annotation { "Feature Type Name" : "Feature", "Feature Type Description" : "" }
export const myFeature = defineFeature(function(context is Context, id is Id, definition is map)
    precondition{}
    {
        {
            var Q0;
            Q0=qCreatedBy(makeId("Top.planeOp"),FACE);
            var sketch = newSketch(context, id + "F0", { "sketchPlane" : qUnion([Q0])});
            skLineSegment(sketch, "E0.bottom", {"start": v(-52.22, 35) * mm, "end": v(51.92, 35) * mm});
            skLineSegment(sketch, "E0.top", {"start": v(-52.22, -33.57) * mm, "end": v(51.92, -33.57) * mm});
            skLineSegment(sketch, "E0.left", {"start": v(-52.22, 35) * mm, "end": v(-52.22, -33.57) * mm});
            skLineSegment(sketch, "E0.right", {"start": v(51.92, 35) * mm, "end": v(51.92, -33.57) * mm});
            skPoint(sketch, "E0.middle", {"position": v(-0.15, 0.72) * mm});
            skLineSegment(sketch, "E1.bottom", {"start": v(-48.41, 31.2) * mm, "end": v(48.1, 31.2) * mm});
            skLineSegment(sketch, "E1.top", {"start": v(-48.41, -29.76) * mm, "end": v(48.1, -29.76) * mm});
            skLineSegment(sketch, "E1.left", {"start": v(-48.41, 31.2) * mm, "end": v(-48.41, -29.76) * mm});
            skLineSegment(sketch, "E1.right", {"start": v(48.1, 31.2) * mm, "end": v(48.1, -29.76) * mm});
            skLineSegment(sketch, "E2", {"start": v(-44.6, 35) * mm, "end": v(-44.6, -33.57) * mm, "construction": true});
            skLineSegment(sketch, "E3", {"start": v(44.3, 31.2) * mm, "end": v(44.3, -33.57) * mm, "construction": true});
            skLineSegment(sketch, "E4", {"start": v(-52.22, 27.39) * mm, "end": v(48.1, 27.39) * mm, "construction": true});
            skLineSegment(sketch, "E5", {"start": v(-52.22, -25.95) * mm, "end": v(51.92, -25.95) * mm, "construction": true});
            skLineSegment(sketch, "E6", {"start": v(-52.22, -33.57) * mm, "end": v(-44.6, -25.95) * mm, "construction": true});
            skCircle(sketch, "E7", {"center": v(-48.41, -29.76) * mm, "radius": 1.52 * mm});
            skLineSegment(sketch, "E8", {"start": v(-52.22, 35) * mm, "end": v(-44.6, 27.39) * mm, "construction": true});
            skCircle(sketch, "E9", {"center": v(-48.41, 31.2) * mm, "radius": 1.52 * mm});
            skLineSegment(sketch, "E10", {"start": v(44.3, 27.39) * mm, "end": v(51.92, 35) * mm, "construction": true});
            skCircle(sketch, "E11", {"center": v(48.1, 31.2) * mm, "radius": 1.52 * mm});
            skLineSegment(sketch, "E12", {"start": v(44.3, -25.95) * mm, "end": v(51.92, -33.57) * mm, "construction": true});
            skCircle(sketch, "E13", {"center": v(48.1, -29.76) * mm, "radius": 1.52 * mm});
            skLineSegment(sketch, "E14", {"start": v(22.7, 35) * mm, "end": v(22.7, -33.57) * mm, "construction": true});
            skLineSegment(sketch, "E15", {"start": v(25.25, 35) * mm, "end": v(25.25, -33.57) * mm, "construction": true});
            skLineSegment(sketch, "E16", {"start": v(26.52, 35) * mm, "end": v(26.52, -33.57) * mm, "construction": true});
            skLineSegment(sketch, "E17", {"start": v(29.06, 35) * mm, "end": v(29.06, -33.57) * mm, "construction": true});
            skLineSegment(sketch, "E18", {"start": v(2.9, 19.77) * mm, "end": v(24.07, 19.77) * mm, "construction": true});
            skLineSegment(sketch, "E19", {"start": v(4.23, -24.68) * mm, "end": v(25.24, -24.68) * mm, "construction": true});
            skLineSegment(sketch, "E20", {"start": v(22.7, -29.76) * mm, "end": v(22.7, -24.68) * mm});
            skLineSegment(sketch, "E21", {"start": v(25.25, -29.76) * mm, "end": v(25.25, -24.68) * mm});
            skLineSegment(sketch, "E22", {"start": v(25.25, -24.68) * mm, "end": v(29.06, -20.87) * mm});
            skLineSegment(sketch, "E23", {"start": v(22.7, -24.68) * mm, "end": v(26.52, -20.87) * mm});
            skLineSegment(sketch, "E24", {"start": v(22.7, 31.2) * mm, "end": v(22.7, 19.77) * mm});
            skLineSegment(sketch, "E25", {"start": v(25.25, 31.2) * mm, "end": v(25.25, 19.77) * mm});
            skLineSegment(sketch, "E26", {"start": v(25.25, 19.77) * mm, "end": v(29.06, 15.96) * mm});
            skLineSegment(sketch, "E27", {"start": v(22.7, 19.77) * mm, "end": v(26.52, 15.96) * mm});
            skLineSegment(sketch, "E28", {"start": v(26.52, 15.96) * mm, "end": v(26.52, -20.87) * mm});
            skLineSegment(sketch, "E29", {"start": v(29.06, 15.96) * mm, "end": v(29.06, -20.87) * mm});
            skLineSegment(sketch, "E30", {"start": v(-44.6, 31.2) * mm, "end": v(-44.6, 27.39) * mm});
            skLineSegment(sketch, "E31", {"start": v(-44.6, 27.39) * mm, "end": v(-48.41, 27.39) * mm});
            skLineSegment(sketch, "E32", {"start": v(-44.6, -29.76) * mm, "end": v(-44.6, -25.95) * mm});
            skLineSegment(sketch, "E33", {"start": v(-44.6, -25.95) * mm, "end": v(-48.41, -25.95) * mm});
            skLineSegment(sketch, "E34", {"start": v(44.3, -29.76) * mm, "end": v(44.3, -25.95) * mm});
            skLineSegment(sketch, "E35", {"start": v(44.3, -25.95) * mm, "end": v(48.1, -25.95) * mm});
            skLineSegment(sketch, "E36", {"start": v(44.3, 31.2) * mm, "end": v(44.3, 27.39) * mm});
            skLineSegment(sketch, "E37", {"start": v(44.3, 27.39) * mm, "end": v(48.1, 27.39) * mm});
            skSolve(sketch);
        }
        {
            var Q0;
            Q0=makeQuery(id+"F0.imprint","IMPRINT",FACE,{"disambiguationData":[TD([[makeQuery(id+"F0.imprint","IMPRINT",EDGE,{"derivedFrom":sQuery(id+"F0.wireOp",EDGE,"E0.bottom")}),-1.0]])]});
            var Q1;
            {var subQ7=sQuery(id+"F0.wireOp",EDGE,"E20");Q1=makeQuery(id+"F0.imprint","IMPRINT",FACE,{"disambiguationData":[TD([[makeQuery(id+"F0.imprint","IMPRINT",EDGE,{"derivedFrom":subQ7}),1.0]])]});}
            var Q2;
            {var subQ5=sQuery(id+"F0.wireOp",EDGE,"E21");Q2=makeQuery(id+"F0.imprint","IMPRINT",FACE,{"disambiguationData":[TD([[makeQuery(id+"F0.imprint","IMPRINT",EDGE,{"derivedFrom":subQ5}),-1.0]])]});}
            var Q3;
            {var subQ2=sQuery(id+"F0.wireOp",EDGE,"E20");Q3=makeQuery(id+"F0.imprint","IMPRINT",FACE,{"disambiguationData":[TD([[makeQuery(id+"F0.imprint","IMPRINT",EDGE,{"derivedFrom":subQ2}),-1.0]])]});}
            var Q4;
            {var subQ0=sQuery(id+"F0.wireOp",EDGE,"E32");Q4=makeQuery(id+"F0.imprint","IMPRINT",FACE,{"disambiguationData":[TD([[makeQuery(id+"F0.imprint","IMPRINT",EDGE,{"derivedFrom":subQ0}),1.0]])]});}
            var Q5;
            {var subQ0=sQuery(id+"F0.wireOp",EDGE,"E34");Q5=makeQuery(id+"F0.imprint","IMPRINT",FACE,{"disambiguationData":[TD([[makeQuery(id+"F0.imprint","IMPRINT",EDGE,{"derivedFrom":subQ0}),-1.0]])]});}
            var Q6;
            {var subQ0=sQuery(id+"F0.wireOp",EDGE,"E30");Q6=makeQuery(id+"F0.imprint","IMPRINT",FACE,{"disambiguationData":[TD([[makeQuery(id+"F0.imprint","IMPRINT",EDGE,{"derivedFrom":subQ0}),-1.0]])]});}
            var Q7;
            {var subQ0=sQuery(id+"F0.wireOp",EDGE,"E36");Q7=makeQuery(id+"F0.imprint","IMPRINT",FACE,{"disambiguationData":[TD([[makeQuery(id+"F0.imprint","IMPRINT",EDGE,{"derivedFrom":subQ0}),1.0]])]});}
            extrude(context, id + "F1", {"entities" : qUnion([Q0, Q1, Q2, Q3, Q4, Q5, Q6, Q7]), "depth" : 3.8 * mm});
        }
        {
            var Q0;
            Q0=makeQuery(id+"F1.opExtrude","SWEPT_EDGE",EDGE,{"disambiguationData":[OSD([sQuery(id+"F0.wireOp",EDGE,"E0.top"),sQuery(id+"F0.wireOp",EDGE,"E0.left")])]});
            var Q1;
            Q1=makeQuery(id+"F1.opExtrude","SWEPT_EDGE",EDGE,{"disambiguationData":[OSD([sQuery(id+"F0.wireOp",EDGE,"E0.bottom"),sQuery(id+"F0.wireOp",EDGE,"E0.left")])]});
            var Q2;
            Q2=makeQuery(id+"F1.opExtrude","SWEPT_EDGE",EDGE,{"disambiguationData":[OSD([sQuery(id+"F0.wireOp",EDGE,"E0.top"),sQuery(id+"F0.wireOp",EDGE,"E0.right")])]});
            var Q3;
            Q3=makeQuery(id+"F1.opExtrude","SWEPT_EDGE",EDGE,{"disambiguationData":[OSD([sQuery(id+"F0.wireOp",EDGE,"E0.bottom"),sQuery(id+"F0.wireOp",EDGE,"E0.right")])]});
            fillet(context, id + "F2", {"entities" : qUnion([Q0, Q1, Q2, Q3]), "radius" : 3.8 * mm, "tangentPropagation" : true, "allowEdgeOverflow" : false});
        }
        {
            var Q0;
            Q0=makeQuery(id+"F1.opExtrude","CAP_FACE",FACE,{"disambiguationData":[OSD([sQuery(id+"F0.wireOp",EDGE,"E0.bottom"),sQuery(id+"F0.wireOp",EDGE,"E0.top"),sQuery(id+"F0.wireOp",EDGE,"E0.left"),sQuery(id+"F0.wireOp",EDGE,"E0.right"),sQuery(id+"F0.wireOp",EDGE,"E7"),sQuery(id+"F0.wireOp",EDGE,"E9"),sQuery(id+"F0.wireOp",EDGE,"E11"),sQuery(id+"F0.wireOp",EDGE,"E13")])],"isStart":false});
            var sketch = newSketch(context, id + "F3", { "sketchPlane" : qUnion([Q0])});
            skLineSegment(sketch, "E38", {"start": v(17.63, 32.47) * mm, "end": v(17.63, -31.03) * mm, "construction": true});
            skLineSegment(sketch, "E39", {"start": v(-7.77, 32.47) * mm, "end": v(-7.77, -31.03) * mm, "construction": true});
            skLineSegment(sketch, "E40.bottom", {"start": v(17.63, 29.93) * mm, "end": v(-7.77, 29.93) * mm});
            skLineSegment(sketch, "E40.top", {"start": v(17.63, -28.5) * mm, "end": v(-7.77, -28.5) * mm});
            skLineSegment(sketch, "E40.left", {"start": v(17.63, 29.93) * mm, "end": v(17.63, -28.5) * mm});
            skLineSegment(sketch, "E40.right", {"start": v(-7.77, 29.93) * mm, "end": v(-7.77, -28.5) * mm});
            skCircle(sketch, "E41", {"center": v(4.93, -0.04) * mm, "radius": 5.72 * mm});
            skCircle(sketch, "E42", {"center": v(11.03, -11.98) * mm, "radius": 4.45 * mm});
            skLineSegment(sketch, "E43.top", {"start": v(17.63, -1493.67) * mm, "end": v(42.19, -1493.67) * mm, "construction": true});
            skLineSegment(sketch, "E43.left", {"start": v(17.63, 29.93) * mm, "end": v(17.63, -1493.67) * mm, "construction": true});
            skLineSegment(sketch, "E44.bottom", {"start": v(17.63, 29.93) * mm, "end": v(45.82, 29.93) * mm, "construction": true});
            skLineSegment(sketch, "E44.top", {"start": v(17.63, -28.5) * mm, "end": v(45.82, -28.5) * mm, "construction": true});
            skLineSegment(sketch, "E44.left", {"start": v(17.63, 29.93) * mm, "end": v(17.63, -28.5) * mm, "construction": true});
            skLineSegment(sketch, "E44.right", {"start": v(45.82, 29.93) * mm, "end": v(45.82, -28.5) * mm, "construction": true});
            skLineSegment(sketch, "E45", {"start": v(0, 0) * mm, "end": v(-49.68, 0) * mm, "construction": true});
            skLineSegment(sketch, "E46", {"start": v(-30.28, -31.03) * mm, "end": v(-30.28, 32.47) * mm, "construction": true});
            skArc(sketch, "E47", {"start": v(-20.12, -16.32) * mm, "mid": v(-11.05, 0) * mm, "end": v(-20.12, 16.32) * mm});
            skLineSegment(sketch, "E48", {"start": v(-25.55, 32.47) * mm, "end": v(-25.55, -31.03) * mm, "construction": true});
            skLineSegment(sketch, "E49", {"start": v(-20.12, 32.47) * mm, "end": v(-20.12, -31.03) * mm, "construction": true});
            skLineSegment(sketch, "E50", {"start": v(-20.12, 16.32) * mm, "end": v(-25.55, 18.64) * mm});
            skLineSegment(sketch, "E51", {"start": v(-25.55, 18.64) * mm, "end": v(-25.55, -18.64) * mm});
            skLineSegment(sketch, "E52", {"start": v(-20.12, -16.32) * mm, "end": v(-25.55, -18.64) * mm});
            skLineSegment(sketch, "E53", {"start": v(-25.55, -18.64) * mm, "end": v(-25.55, 18.64) * mm});
            skLineSegment(sketch, "E54", {"start": v(-18.76, 20.32) * mm, "end": v(-52.32, 20.32) * mm, "construction": true});
            skLineSegment(sketch, "E55", {"start": v(-17.13, -20.3) * mm, "end": v(-51.17, -20.3) * mm, "construction": true});
            skLineSegment(sketch, "E56", {"start": v(-18.66, 19.05) * mm, "end": v(-52.32, 19.05) * mm, "construction": true});
            skLineSegment(sketch, "E57", {"start": v(-17.13, -19.04) * mm, "end": v(-51.17, -19.04) * mm, "construction": true});
            skLineSegment(sketch, "E58", {"start": v(-28.27, 19.05) * mm, "end": v(-28.27, -19.04) * mm});
            skPoint(sketch, "E58.endSnap0", {"position": v(-34.15, -19.04) * mm});
            skLineSegment(sketch, "E59", {"start": v(-29.28, 20.32) * mm, "end": v(-29.28, -20.3) * mm});
            skLineSegment(sketch, "E60", {"start": v(-29.28, 20.32) * mm, "end": v(-28.27, 19.05) * mm});
            skLineSegment(sketch, "E61", {"start": v(-29.28, -20.3) * mm, "end": v(-28.27, -19.04) * mm});
            skLineSegment(sketch, "E62", {"start": v(-34.72, 19.05) * mm, "end": v(-34.72, -19.04) * mm});
            skLineSegment(sketch, "E63", {"start": v(-35.74, 20.32) * mm, "end": v(-35.74, -20.3) * mm});
            skLineSegment(sketch, "E64", {"start": v(-35.74, 20.32) * mm, "end": v(-34.72, 19.05) * mm});
            skLineSegment(sketch, "E65", {"start": v(-35.74, -20.3) * mm, "end": v(-34.72, -19.04) * mm});
            skLineSegment(sketch, "E66", {"start": v(-41.17, 19.05) * mm, "end": v(-41.17, -19.04) * mm});
            skLineSegment(sketch, "E67", {"start": v(-42.19, 20.32) * mm, "end": v(-42.19, -20.3) * mm});
            skLineSegment(sketch, "E68", {"start": v(-25.55, 17.48) * mm, "end": v(-41.17, 17.48) * mm, "construction": true});
            skPoint(sketch, "E68.startSnap0", {"position": v(-22.83, 17.48) * mm});
            skLineSegment(sketch, "E69", {"start": v(-25.55, -17) * mm, "end": v(-41.17, -17) * mm, "construction": true});
            skLineSegment(sketch, "E70", {"start": v(-25.55, 0) * mm, "end": v(-14.8, 15.93) * mm, "construction": true});
            skLineSegment(sketch, "E71", {"start": v(-25.55, 0) * mm, "end": v(-14.96, -15.7) * mm, "construction": true});
            skCircle(sketch, "E72", {"center": v(-16.5, -13.42) * mm, "radius": 1.9 * mm});
            skCircle(sketch, "E73", {"center": v(-16.5, 13.42) * mm, "radius": 1.9 * mm});
            skLineSegment(sketch, "E74.bottom", {"start": v(-16.58, -1.47) * mm, "end": v(-23.65, -1.47) * mm});
            skLineSegment(sketch, "E74.top", {"start": v(-16.58, 1.47) * mm, "end": v(-23.65, 1.47) * mm});
            skLineSegment(sketch, "E74.left", {"start": v(-16.58, -1.47) * mm, "end": v(-16.58, 1.47) * mm});
            skLineSegment(sketch, "E74.right", {"start": v(-23.65, -1.47) * mm, "end": v(-23.65, 1.47) * mm});
            skPoint(sketch, "E74.middle", {"position": v(-20.12, 0) * mm});
            skLineSegment(sketch, "E75", {"start": v(-25.55, 17.48) * mm, "end": v(-28.27, 17.48) * mm});
            skLineSegment(sketch, "E76", {"start": v(-25.55, -17) * mm, "end": v(-28.27, -17) * mm});
            skLineSegment(sketch, "E77", {"start": v(-29.28, -17) * mm, "end": v(-34.72, -17) * mm});
            skLineSegment(sketch, "E78", {"start": v(-35.67, -17) * mm, "end": v(-41.17, -17) * mm});
            skLineSegment(sketch, "E79", {"start": v(-29.28, 17.48) * mm, "end": v(-34.72, 17.48) * mm});
            skLineSegment(sketch, "E80", {"start": v(-35.74, 17.48) * mm, "end": v(-41.17, 17.48) * mm});
            skLineSegment(sketch, "E81", {"start": v(-42.19, 20.32) * mm, "end": v(-41.17, 19.05) * mm});
            skLineSegment(sketch, "E82", {"start": v(-42.19, -20.3) * mm, "end": v(-41.17, -19.04) * mm});
            skLineSegment(sketch, "E83", {"start": v(-42.19, 20.32) * mm, "end": v(-54.89, 20.3) * mm, "construction": true});
            skLineSegment(sketch, "E84", {"start": v(-42.19, -20.3) * mm, "end": v(-58.7, -20.3) * mm, "construction": true});
            skCircle(sketch, "E85", {"center": v(4.93, 15.2) * mm, "radius": 3.81 * mm});
            skLineSegment(sketch, "E86", {"start": v(4.93, 15.2) * mm, "end": v(17.63, 15.2) * mm, "construction": true});
            skLineSegment(sketch, "E87", {"start": v(4.93, -0.04) * mm, "end": v(17.63, -0.04) * mm, "construction": true});
            skLineSegment(sketch, "E88", {"start": v(4.93, -0.04) * mm, "end": v(4.93, 29.93) * mm, "construction": true});
            skText(sketch, "E89", { "text": "Dalek Voice Changer", "fontName": "OpenSans-Regular.ttf"});
            skText(sketch, "E90", { "text": "Exterminate!", "fontName": "OpenSans-Regular.ttf"});
            skLineSegment(sketch, "E91", {"start": v(35.1, 29.93) * mm, "end": v(35.1, -28.5) * mm, "construction": true});
            skLineSegment(sketch, "E92", {"start": v(-48.41, 31.2) * mm, "end": v(-48.41, -29.76) * mm, "construction": true});
            skLineSegment(sketch, "E93", {"start": v(-48.41, -29.76) * mm, "end": v(48.1, -29.76) * mm, "construction": true});
            skLineSegment(sketch, "E94", {"start": v(48.1, -29.76) * mm, "end": v(48.1, 31.2) * mm, "construction": true});
            skLineSegment(sketch, "E95", {"start": v(-48.41, 31.2) * mm, "end": v(48.1, 31.2) * mm, "construction": true});
            const initialGuessF3  = {"E89": [0.04145, 0.02993, 0, -1, 0.00437], "E90": [0.028, 0.02993, 0, -1, 0.0071]};
            skSetInitialGuess(sketch, initialGuessF3);
            skSolve(sketch);
        }
        {
            var Q0;
            Q0=makeQuery(id+"F3.imprint","IMPRINT",FACE,{"disambiguationData":[TD([[makeQuery(id+"F3.imprint","IMPRINT",EDGE,{"derivedFrom":sQuery(id+"F3.wireOp",EDGE,"E40.bottom")}),1.0]])]});
            var Q1;
            Q1=makeQuery(id+"F3.imprint","IMPRINT",FACE,{"disambiguationData":[TD([[makeQuery(id+"F3.imprint","IMPRINT",EDGE,{"derivedFrom":sQuery(id+"F3.wireOp",EDGE,"E41")}),1.0]])]});
            var Q2;
            Q2=makeQuery(id+"F3.imprint","IMPRINT",FACE,{"disambiguationData":[TD([[makeQuery(id+"F3.imprint","IMPRINT",EDGE,{"derivedFrom":sQuery(id+"F3.wireOp",EDGE,"E42")}),1.0]])]});
            extrude(context, id + "F4", {"entities" : qUnion([Q0, Q1, Q2]), "operationType" : NewBodyOperationType.REMOVE, "oppositeDirection" : true, "depth" : .66 * mm});
        }
        {
            var Q0;
            Q0=makeQuery(id+"F3.imprint","IMPRINT",FACE,{"disambiguationData":[TD([[makeQuery(id+"F3.imprint","IMPRINT",EDGE,{"derivedFrom":sQuery(id+"F3.wireOp",EDGE,"E41")}),1.0]])]});
            var Q1;
            Q1=makeQuery(id+"F3.imprint","IMPRINT",FACE,{"disambiguationData":[TD([[makeQuery(id+"F3.imprint","IMPRINT",EDGE,{"derivedFrom":sQuery(id+"F3.wireOp",EDGE,"E42")}),1.0]])]});
            var Q2;
            Q2=makeQuery(id+"F3.imprint","IMPRINT",FACE,{"disambiguationData":[TD([[makeQuery(id+"F3.imprint","IMPRINT",EDGE,{"derivedFrom":sQuery(id+"F3.wireOp",EDGE,"E85")}),1.0]])]});
            extrude(context, id + "F5", {"entities" : qUnion([Q0, Q1, Q2]), "operationType" : NewBodyOperationType.REMOVE, "oppositeDirection" : true, "depth" : 25.4 * mm});
        }
        {
            var Q0;
            {var subQ0=sQuery(id+"F3.wireOp",EDGE,"E60");Q0=makeQuery(id+"F3.imprint","IMPRINT",FACE,{"disambiguationData":[TD([[makeQuery(id+"F3.imprint","IMPRINT",EDGE,{"derivedFrom":subQ0}),-1.0]])]});}
            var Q1;
            {var subQ0=sQuery(id+"F3.wireOp",EDGE,"E64");Q1=makeQuery(id+"F3.imprint","IMPRINT",FACE,{"disambiguationData":[TD([[makeQuery(id+"F3.imprint","IMPRINT",EDGE,{"derivedFrom":subQ0}),-1.0]])]});}
            var Q2;
            Q2=makeQuery(id+"F3.imprint","IMPRINT",FACE,{"disambiguationData":[TD([[makeQuery(id+"F3.imprint","IMPRINT",EDGE,{"derivedFrom":sQuery(id+"F3.wireOp",EDGE,"E67")}),1.0]])]});
            var Q3;
            {var subQ7=sQuery(id+"F3.wireOp",EDGE,"E50");Q3=makeQuery(id+"F3.imprint","IMPRINT",FACE,{"disambiguationData":[TD([[makeQuery(id+"F3.imprint","IMPRINT",EDGE,{"derivedFrom":subQ7}),1.0]])]});}
            var Q4;
            {var subQ0=sQuery(id+"F3.wireOp",EDGE,"E73");var subQ1=sQuery(id+"F3.wireOp",EDGE,"E47");var subQ2=makeQuery(id+"F3.imprint","INTERSECT",VERTEX,{"disambiguationData":[OD(0.0)],"derivedFrom":[subQ1,subQ0]});Q4=makeQuery(id+"F3.imprint","IMPRINT",FACE,{"disambiguationData":[TD([[makeQuery(id+"F3.imprint","IMPRINT",EDGE,{"disambiguationData":[TD([[subQ2,-1.0]])],"derivedFrom":subQ1}),-1.0]])]});}
            var Q5;
            {var subQ0=sQuery(id+"F3.wireOp",EDGE,"E72");var subQ1=sQuery(id+"F3.wireOp",EDGE,"E47");var subQ2=makeQuery(id+"F3.imprint","INTERSECT",VERTEX,{"disambiguationData":[OD(0.0)],"derivedFrom":[subQ1,subQ0]});Q5=makeQuery(id+"F3.imprint","IMPRINT",FACE,{"disambiguationData":[TD([[makeQuery(id+"F3.imprint","IMPRINT",EDGE,{"disambiguationData":[TD([[subQ2,-1.0]])],"derivedFrom":subQ1}),-1.0]])]});}
            var Q6;
            {var subQ0=sQuery(id+"F3.wireOp",EDGE,"E72");var subQ1=sQuery(id+"F3.wireOp",EDGE,"E47");var subQ2=makeQuery(id+"F3.imprint","INTERSECT",VERTEX,{"disambiguationData":[OD(0.0)],"derivedFrom":[subQ1,subQ0]});Q6=makeQuery(id+"F3.imprint","IMPRINT",FACE,{"disambiguationData":[TD([[makeQuery(id+"F3.imprint","IMPRINT",EDGE,{"disambiguationData":[TD([[subQ2,-1.0]])],"derivedFrom":subQ1}),1.0]])]});}
            var Q7;
            {var subQ0=sQuery(id+"F3.wireOp",EDGE,"E73");var subQ1=sQuery(id+"F3.wireOp",EDGE,"E47");var subQ2=makeQuery(id+"F3.imprint","INTERSECT",VERTEX,{"disambiguationData":[OD(0.0)],"derivedFrom":[subQ1,subQ0]});Q7=makeQuery(id+"F3.imprint","IMPRINT",FACE,{"disambiguationData":[TD([[makeQuery(id+"F3.imprint","IMPRINT",EDGE,{"disambiguationData":[TD([[subQ2,-1.0]])],"derivedFrom":subQ1}),1.0]])]});}
            var Q8;
            Q8=makeQuery(id+"F3.imprint","IMPRINT",FACE,{"disambiguationData":[TD([[makeQuery(id+"F3.imprint","IMPRINT",EDGE,{"derivedFrom":sQuery(id+"F3.wireOp",EDGE,"E90.sketch_text.stroke-0")}),-1.0]])]});
            var Q9;
            Q9=makeQuery(id+"F3.imprint","IMPRINT",FACE,{"disambiguationData":[TD([[makeQuery(id+"F3.imprint","IMPRINT",EDGE,{"derivedFrom":sQuery(id+"F3.wireOp",EDGE,"E90.sketch_text.stroke-12")}),-1.0]])]});
            var Q10;
            Q10=makeQuery(id+"F3.imprint","IMPRINT",FACE,{"disambiguationData":[TD([[makeQuery(id+"F3.imprint","IMPRINT",EDGE,{"derivedFrom":sQuery(id+"F3.wireOp",EDGE,"E90.sketch_text.stroke-24")}),-1.0]])]});
            var Q11;
            Q11=makeQuery(id+"F3.imprint","IMPRINT",FACE,{"disambiguationData":[TD([[makeQuery(id+"F3.imprint","IMPRINT",EDGE,{"derivedFrom":sQuery(id+"F3.wireOp",EDGE,"E89.sketch_text.stroke-0")}),-1.0]])]});
            var Q12;
            Q12=makeQuery(id+"F3.imprint","IMPRINT",FACE,{"disambiguationData":[TD([[makeQuery(id+"F3.imprint","IMPRINT",EDGE,{"derivedFrom":sQuery(id+"F3.wireOp",EDGE,"E89.sketch_text.stroke-14")}),-1.0]])]});
            var Q13;
            Q13=makeQuery(id+"F3.imprint","IMPRINT",FACE,{"disambiguationData":[TD([[makeQuery(id+"F3.imprint","IMPRINT",EDGE,{"derivedFrom":sQuery(id+"F3.wireOp",EDGE,"E89.sketch_text.stroke-41")}),-1.0]])]});
            var Q14;
            Q14=makeQuery(id+"F3.imprint","IMPRINT",FACE,{"disambiguationData":[TD([[makeQuery(id+"F3.imprint","IMPRINT",EDGE,{"derivedFrom":sQuery(id+"F3.wireOp",EDGE,"E89.sketch_text.stroke-45")}),-1.0]])]});
            var Q15;
            Q15=makeQuery(id+"F3.imprint","IMPRINT",FACE,{"disambiguationData":[TD([[makeQuery(id+"F3.imprint","IMPRINT",EDGE,{"derivedFrom":sQuery(id+"F3.wireOp",EDGE,"E89.sketch_text.stroke-64")}),-1.0]])]});
            var Q16;
            Q16=makeQuery(id+"F3.imprint","IMPRINT",FACE,{"disambiguationData":[TD([[makeQuery(id+"F3.imprint","IMPRINT",EDGE,{"derivedFrom":sQuery(id+"F3.wireOp",EDGE,"E90.sketch_text.stroke-43")}),-1.0]])]});
            var Q17;
            Q17=makeQuery(id+"F3.imprint","IMPRINT",FACE,{"disambiguationData":[TD([[makeQuery(id+"F3.imprint","IMPRINT",EDGE,{"derivedFrom":sQuery(id+"F3.wireOp",EDGE,"E89.sketch_text.stroke-79")}),-1.0]])]});
            var Q18;
            Q18=makeQuery(id+"F3.imprint","IMPRINT",FACE,{"disambiguationData":[TD([[makeQuery(id+"F3.imprint","IMPRINT",EDGE,{"derivedFrom":sQuery(id+"F3.wireOp",EDGE,"E89.sketch_text.stroke-88")}),-1.0]])]});
            var Q19;
            Q19=makeQuery(id+"F3.imprint","IMPRINT",FACE,{"disambiguationData":[TD([[makeQuery(id+"F3.imprint","IMPRINT",EDGE,{"derivedFrom":sQuery(id+"F3.wireOp",EDGE,"E89.sketch_text.stroke-105")}),-1.0]])]});
            var Q20;
            Q20=makeQuery(id+"F3.imprint","IMPRINT",FACE,{"disambiguationData":[TD([[makeQuery(id+"F3.imprint","IMPRINT",EDGE,{"derivedFrom":sQuery(id+"F3.wireOp",EDGE,"E89.sketch_text.stroke-109")}),-1.0]])]});
            var Q21;
            Q21=makeQuery(id+"F3.imprint","IMPRINT",FACE,{"disambiguationData":[TD([[makeQuery(id+"F3.imprint","IMPRINT",EDGE,{"derivedFrom":sQuery(id+"F3.wireOp",EDGE,"E89.sketch_text.stroke-117")}),-1.0]])]});
            var Q22;
            Q22=makeQuery(id+"F3.imprint","IMPRINT",FACE,{"disambiguationData":[TD([[makeQuery(id+"F3.imprint","IMPRINT",EDGE,{"derivedFrom":sQuery(id+"F3.wireOp",EDGE,"E89.sketch_text.stroke-132")}),-1.0]])]});
            var Q23;
            Q23=makeQuery(id+"F3.imprint","IMPRINT",FACE,{"disambiguationData":[TD([[makeQuery(id+"F3.imprint","IMPRINT",EDGE,{"derivedFrom":sQuery(id+"F3.wireOp",EDGE,"E90.sketch_text.stroke-62")}),-1.0]])]});
            var Q24;
            Q24=makeQuery(id+"F3.imprint","IMPRINT",FACE,{"disambiguationData":[TD([[makeQuery(id+"F3.imprint","IMPRINT",EDGE,{"derivedFrom":sQuery(id+"F3.wireOp",EDGE,"E90.sketch_text.stroke-75")}),-1.0]])]});
            var Q25;
            Q25=makeQuery(id+"F3.imprint","IMPRINT",FACE,{"disambiguationData":[TD([[makeQuery(id+"F3.imprint","IMPRINT",EDGE,{"derivedFrom":sQuery(id+"F3.wireOp",EDGE,"E90.sketch_text.stroke-103")}),-1.0]])]});
            var Q26;
            Q26=makeQuery(id+"F3.imprint","IMPRINT",FACE,{"disambiguationData":[TD([[makeQuery(id+"F3.imprint","IMPRINT",EDGE,{"derivedFrom":sQuery(id+"F3.wireOp",EDGE,"E90.sketch_text.stroke-107")}),-1.0]])]});
            var Q27;
            Q27=makeQuery(id+"F3.imprint","IMPRINT",FACE,{"disambiguationData":[TD([[makeQuery(id+"F3.imprint","IMPRINT",EDGE,{"derivedFrom":sQuery(id+"F3.wireOp",EDGE,"E90.sketch_text.stroke-115")}),-1.0]])]});
            var Q28;
            Q28=makeQuery(id+"F3.imprint","IMPRINT",FACE,{"disambiguationData":[TD([[makeQuery(id+"F3.imprint","IMPRINT",EDGE,{"derivedFrom":sQuery(id+"F3.wireOp",EDGE,"E90.sketch_text.stroke-132")}),-1.0]])]});
            var Q29;
            Q29=makeQuery(id+"F3.imprint","IMPRINT",FACE,{"disambiguationData":[TD([[makeQuery(id+"F3.imprint","IMPRINT",EDGE,{"derivedFrom":sQuery(id+"F3.wireOp",EDGE,"E90.sketch_text.stroke-159")}),-1.0]])]});
            var Q30;
            Q30=makeQuery(id+"F3.imprint","IMPRINT",FACE,{"disambiguationData":[TD([[makeQuery(id+"F3.imprint","IMPRINT",EDGE,{"derivedFrom":sQuery(id+"F3.wireOp",EDGE,"E90.sketch_text.stroke-178")}),-1.0]])]});
            var Q31;
            Q31=makeQuery(id+"F3.imprint","IMPRINT",FACE,{"disambiguationData":[TD([[makeQuery(id+"F3.imprint","IMPRINT",EDGE,{"derivedFrom":sQuery(id+"F3.wireOp",EDGE,"E90.sketch_text.stroke-197")}),-1.0]])]});
            var Q32;
            Q32=makeQuery(id+"F3.imprint","IMPRINT",FACE,{"disambiguationData":[TD([[makeQuery(id+"F3.imprint","IMPRINT",EDGE,{"derivedFrom":sQuery(id+"F3.wireOp",EDGE,"E90.sketch_text.stroke-201")}),-1.0]])]});
            var Q33;
            Q33=makeQuery(id+"F3.imprint","IMPRINT",FACE,{"disambiguationData":[TD([[makeQuery(id+"F3.imprint","IMPRINT",EDGE,{"derivedFrom":sQuery(id+"F3.wireOp",EDGE,"E89.sketch_text.stroke-151")}),-1.0]])]});
            var Q34;
            Q34=makeQuery(id+"F3.imprint","IMPRINT",FACE,{"disambiguationData":[TD([[makeQuery(id+"F3.imprint","IMPRINT",EDGE,{"derivedFrom":sQuery(id+"F3.wireOp",EDGE,"E89.sketch_text.stroke-166")}),-1.0]])]});
            var Q35;
            Q35=makeQuery(id+"F3.imprint","IMPRINT",FACE,{"disambiguationData":[TD([[makeQuery(id+"F3.imprint","IMPRINT",EDGE,{"derivedFrom":sQuery(id+"F3.wireOp",EDGE,"E89.sketch_text.stroke-184")}),-1.0]])]});
            var Q36;
            Q36=makeQuery(id+"F3.imprint","IMPRINT",FACE,{"disambiguationData":[TD([[makeQuery(id+"F3.imprint","IMPRINT",EDGE,{"derivedFrom":sQuery(id+"F3.wireOp",EDGE,"E89.sketch_text.stroke-211")}),-1.0]])]});
            var Q37;
            Q37=makeQuery(id+"F3.imprint","IMPRINT",FACE,{"disambiguationData":[TD([[makeQuery(id+"F3.imprint","IMPRINT",EDGE,{"derivedFrom":sQuery(id+"F3.wireOp",EDGE,"E89.sketch_text.stroke-228")}),-1.0]])]});
            var Q38;
            Q38=makeQuery(id+"F3.imprint","IMPRINT",FACE,{"disambiguationData":[TD([[makeQuery(id+"F3.imprint","IMPRINT",EDGE,{"derivedFrom":sQuery(id+"F3.wireOp",EDGE,"E89.sketch_text.stroke-272")}),-1.0]])]});
            var Q39;
            Q39=makeQuery(id+"F3.imprint","IMPRINT",FACE,{"disambiguationData":[TD([[makeQuery(id+"F3.imprint","IMPRINT",EDGE,{"derivedFrom":sQuery(id+"F3.wireOp",EDGE,"E89.sketch_text.stroke-291")}),-1.0]])]});
            extrude(context, id + "F6", {"entities" : qUnion([Q0, Q1, Q2, Q3, Q4, Q5, Q6, Q7, Q8, Q9, Q10, Q11, Q12, Q13, Q14, Q15, Q16, Q17, Q18, Q19, Q20, Q21, Q22, Q23, Q24, Q25, Q26, Q27, Q28, Q29, Q30, Q31, Q32, Q33, Q34, Q35, Q36, Q37, Q38, Q39]), "operationType" : NewBodyOperationType.ADD, "depth" : 1 * mm});
        }
        {
            var Q0;
            {var subQ0=sQuery(id+"F3.wireOp",EDGE,"E75");Q0=makeQuery(id+"F3.imprint","IMPRINT",FACE,{"disambiguationData":[TD([[makeQuery(id+"F3.imprint","IMPRINT",EDGE,{"derivedFrom":subQ0}),1.0]])]});}
            var Q1;
            {var subQ0=sQuery(id+"F3.wireOp",EDGE,"E77");Q1=makeQuery(id+"F3.imprint","IMPRINT",FACE,{"disambiguationData":[TD([[makeQuery(id+"F3.imprint","IMPRINT",EDGE,{"derivedFrom":subQ0}),-1.0]])]});}
            var Q2;
            {var subQ0=sQuery(id+"F3.wireOp",EDGE,"E80");Q2=makeQuery(id+"F3.imprint","IMPRINT",FACE,{"disambiguationData":[TD([[makeQuery(id+"F3.imprint","IMPRINT",EDGE,{"derivedFrom":subQ0}),1.0]])]});}
            extrude(context, id + "F7", {"entities" : qUnion([Q0, Q1, Q2]), "operationType" : NewBodyOperationType.REMOVE, "oppositeDirection" : true, "depth" : .6 * mm});
        }
    });